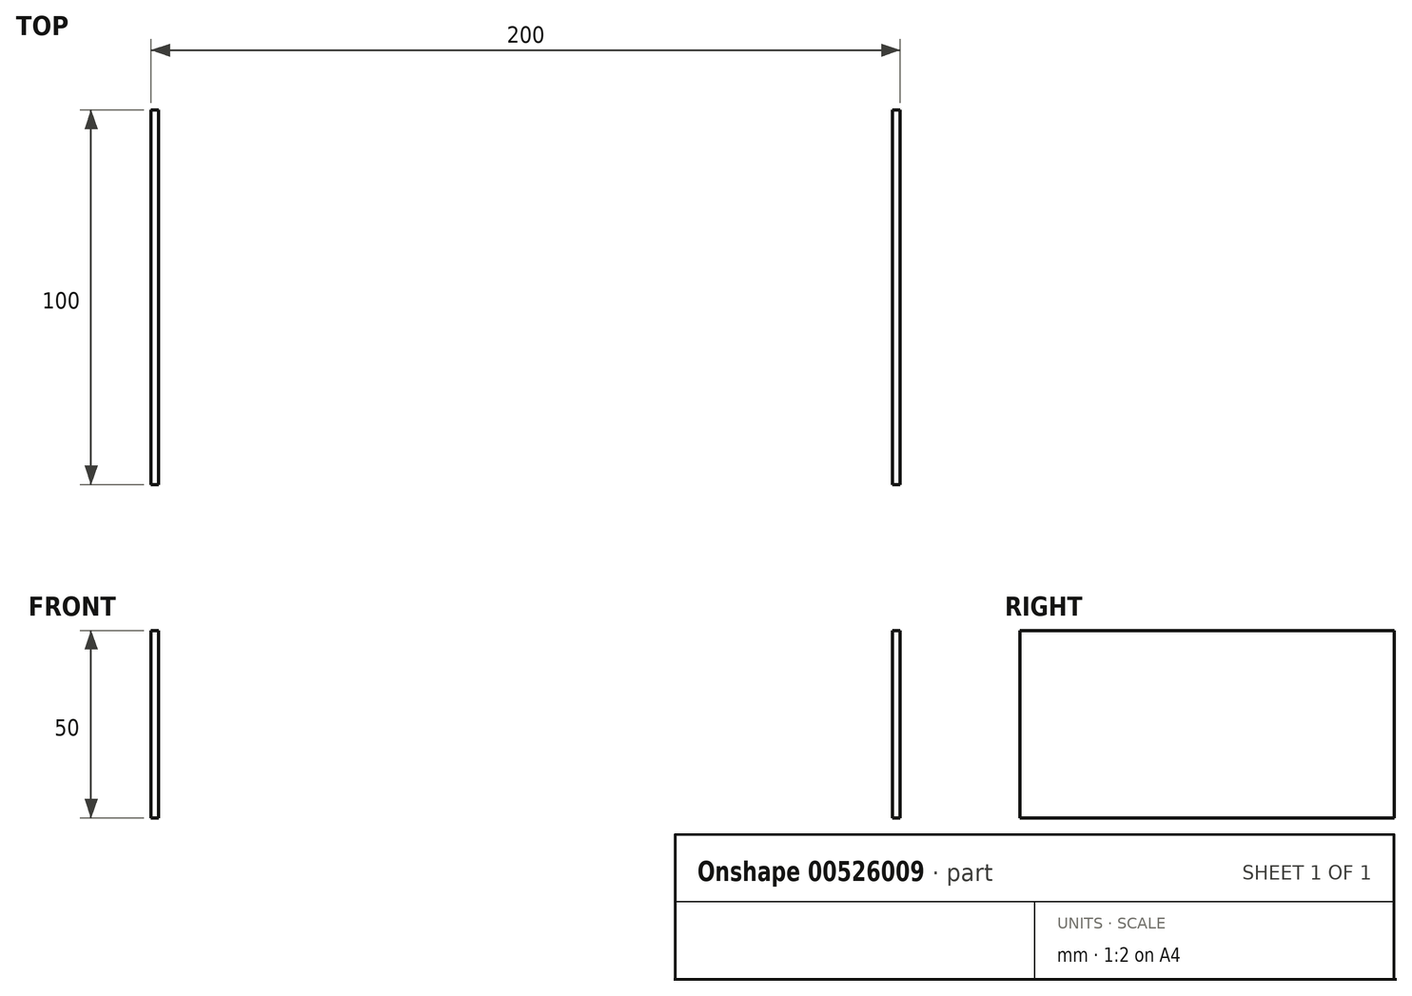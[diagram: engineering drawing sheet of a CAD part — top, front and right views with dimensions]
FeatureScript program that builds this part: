
annotation { "Feature Type Name" : "Feature", "Feature Type Description" : "" }
export const myFeature = defineFeature(function(context is Context, id is Id, definition is map)
    precondition{}
    {
        {
            var Q0;
            Q0=qCreatedBy(makeId("Front.planeOp"),FACE);
            var sketch = newSketch(context, id + "F0", { "sketchPlane" : qUnion([Q0])});
            skLineSegment(sketch, "E0.bottom", {"start": v(-100, 25) * mm, "end": v(100, 25) * mm});
            skLineSegment(sketch, "E0.top", {"start": v(-100, -25) * mm, "end": v(100, -25) * mm});
            skLineSegment(sketch, "E0.left", {"start": v(-100, 25) * mm, "end": v(-100, -25) * mm});
            skLineSegment(sketch, "E0.right", {"start": v(100, 25) * mm, "end": v(100, -25) * mm});
            skPoint(sketch, "E0.middle", {"position": v(0, 0) * mm});
            skLineSegment(sketch, "E1", {"start": v(98, 25) * mm, "end": v(98, -25) * mm});
            skLineSegment(sketch, "E2.MirrorCS", {"start": v(-98, 25) * mm, "end": v(-98, -25) * mm});
            skSolve(sketch);
        }
        {
            var Q0;
            {var subQ0=sQuery(id+"F0.wireOp",EDGE,"E0.left");Q0=makeQuery(id+"F0.imprint","IMPRINT",FACE,{"disambiguationData":[TD([[makeQuery(id+"F0.imprint","IMPRINT",EDGE,{"derivedFrom":subQ0}),1.0]])]});}
            var Q1;
            {var subQ0=sQuery(id+"F0.wireOp",EDGE,"E0.right");Q1=makeQuery(id+"F0.imprint","IMPRINT",FACE,{"disambiguationData":[TD([[makeQuery(id+"F0.imprint","IMPRINT",EDGE,{"derivedFrom":subQ0}),-1.0]])]});}
            extrude(context, id + "F1", {"entities" : qUnion([Q0, Q1]), "depth" : 100 * mm, "offsetDistance" : 25 * mm});
        }
    });
